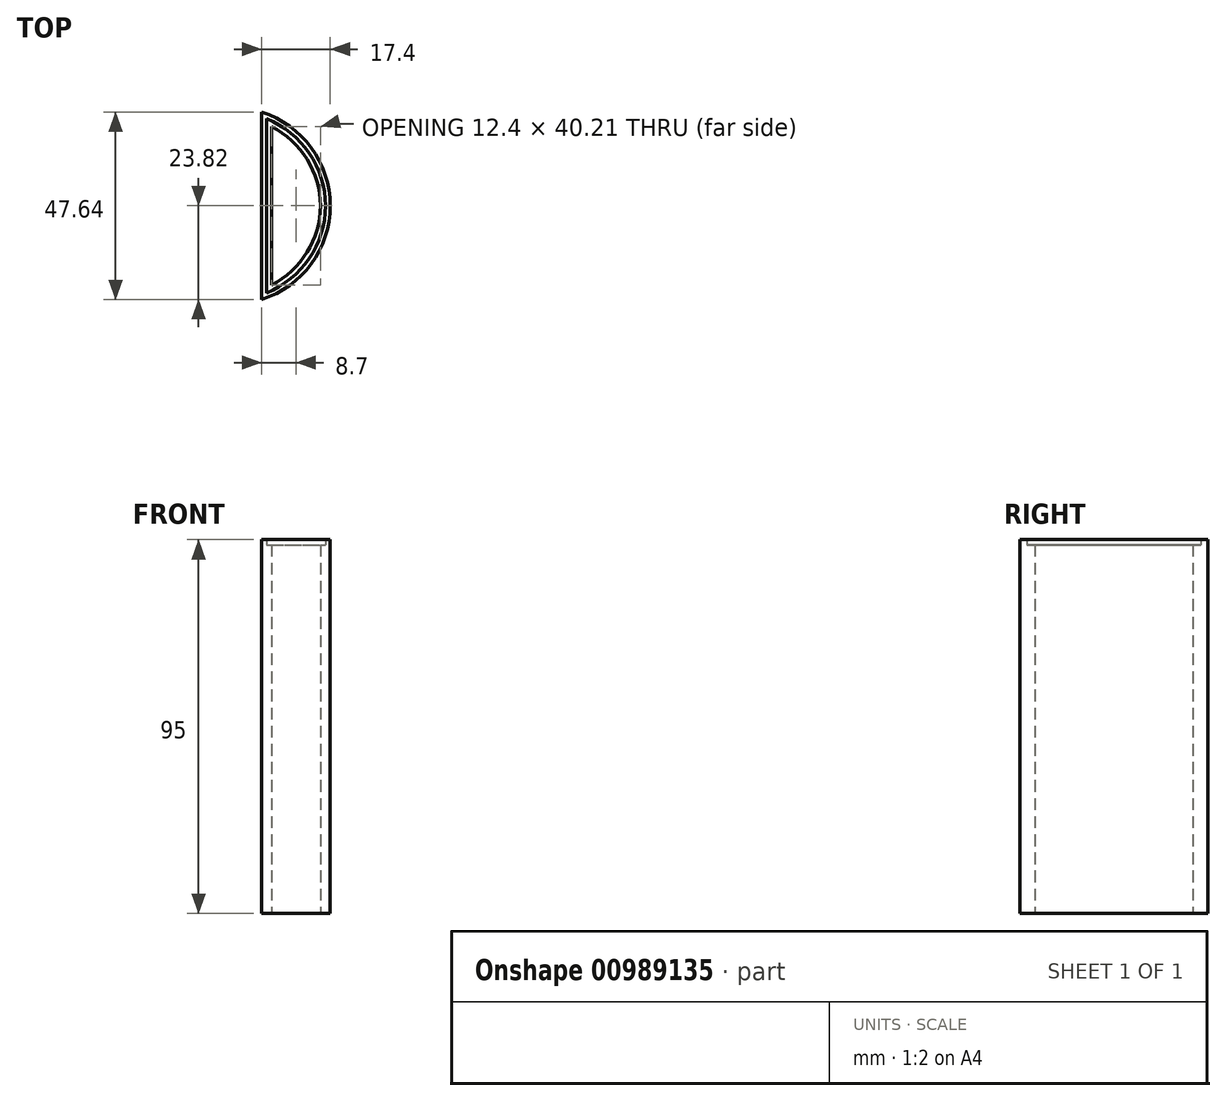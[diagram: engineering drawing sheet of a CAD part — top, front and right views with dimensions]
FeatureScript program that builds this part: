
annotation { "Feature Type Name" : "Feature", "Feature Type Description" : "" }
export const myFeature = defineFeature(function(context is Context, id is Id, definition is map)
    precondition{}
    {
        {
            var Q0;
            Q0=qCreatedBy(makeId("Top.planeOp"),FACE);
            var sketch = newSketch(context, id + "F0", { "sketchPlane" : qUnion([Q0])});
            skArc(sketch, "E0", {"start": v(7.6, -23.82) * mm, "mid": v(25, 0) * mm, "end": v(7.6, 23.82) * mm});
            skArc(sketch, "E1", {"start": v(10.1, -20.1) * mm, "mid": v(22.5, 0) * mm, "end": v(10.1, 20.1) * mm});
            skLineSegment(sketch, "E2", {"start": v(7.6, 21.18) * mm, "end": v(7.6, -21.18) * mm});
            skLineSegment(sketch, "E3", {"start": v(7.6, 21.18) * mm, "end": v(7.6, 23.82) * mm});
            skLineSegment(sketch, "E4", {"start": v(7.6, -21.18) * mm, "end": v(7.6, -23.82) * mm});
            skLineSegment(sketch, "E5", {"start": v(10.1, 20.1) * mm, "end": v(10.1, -20.1) * mm});
            skArc(sketch, "E6", {"start": v(8.8, -22.11) * mm, "mid": v(23.8, 0) * mm, "end": v(8.8, 22.11) * mm});
            skLineSegment(sketch, "E7", {"start": v(8.8, 22.11) * mm, "end": v(8.8, -22.11) * mm});
            skSolve(sketch);
        }
        {
            var Q0;
            Q0=makeQuery(id+"F0.imprint","IMPRINT",FACE,{"disambiguationData":[TD([[makeQuery(id+"F0.imprint","IMPRINT",EDGE,{"derivedFrom":sQuery(id+"F0.wireOp",EDGE,"E0")}),1.0]])]});
            extrude(context, id + "F1", {"entities" : qUnion([Q0]), "depth" : 95 * mm, "offsetDistance" : 25.4 * mm});
        }
        {
            var Q0;
            Q0=makeQuery(id+"F0.imprint","IMPRINT",FACE,{"disambiguationData":[TD([[makeQuery(id+"F0.imprint","IMPRINT",EDGE,{"derivedFrom":sQuery(id+"F0.wireOp",EDGE,"E1")}),-1.0]])]});
            extrude(context, id + "F2", {"entities" : qUnion([Q0]), "operationType" : NewBodyOperationType.ADD, "depth" : 93.7 * mm, "offsetDistance" : 25.4 * mm});
        }
    });
